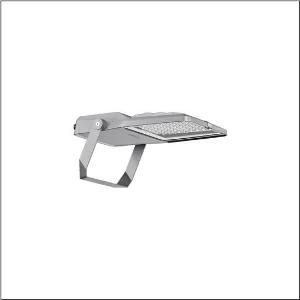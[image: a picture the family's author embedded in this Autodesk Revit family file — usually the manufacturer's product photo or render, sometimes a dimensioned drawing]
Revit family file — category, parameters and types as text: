
# Revit family: floodlight_fl_21_iq_mini___rs12_5xa7771c4b1a_004d
name_source: partatom
category: Lighting Fixtures
units: mm (PartAtom-declared; Revit-internal decimal feet)

## family parameters
Cut with Voids When Loaded = No
Host = Face
Light Source = No
Part Type = Normal
Room Calculation Point = No
Round Connector Dimension = Use Diameter
Shared = No

## types (1)
- --- (1 x LED, 12860 lm, 87.2 W, 4000K)
    Apparent Load = 87 VA
    CIE Flux Codes = 79 92 99 100 100
    Color Rendering = 70
    Color Temperature = 4000K
    Default Elevation = 1800 mm
    Description = Floodlight FL 21 iQ mini, floodlight, primary light control with lens, of PMMA, primary optical cover: protective disc, of toughened safety glass, transparent, light distribution: RS12, light emission: direct distribution, installation type: surface-mounted, LED, High Power LED, rated luminous flux: 12.860lm, luminous efficacy: 148lm/W, light colour: 740, colour temperature: 4000K, control: Auto-Match, Temp-Guard, Lumen-Switch, Night-Set, Smart-Wire, Light-Fading, Desk-Remote (wireless, voltage-free reading and setting of iQ features in the workshop via application-optimized NFC function/RFID function), optimised constant luminous flux control (CLO 2.0), with terminal, 6-pole, mains connection: 220..240V, AC, 50/60Hz, start of lifetime: 87W, end of service life: 92W, reduction: 40W, luminaire housing, of diecast aluminium, powder-coated, Siteco® metallic grey (DB 702S), corrosivity category C5 mid according to DIN EN ISO 12944, sealing non-destructively replaceable, mounting bracket, of steel, galvanised, powder-coated, Siteco® metallic grey (DB 702S), protection rating (complete): IP66, insulation class (complete): insulation class II (safety insulation), certification: CE, ENEC, VDE, protection symbol: D, impact resistance: IK08, permissible operating ambient temperature: -40..+40°C, permissible operating ambient temperature for outdoor applications: -40..+50°C, standard: DIN EN 12944, LABS conformity tested according to VDMA 24364:2018-05, packaging unit: 1 piece

Light Distribution: RS12
    Height = 70 mm
    Lamp = 1 x LED
    Lamp Light Flux = 12860 lm
    Lamp Power = 87.2 W
    Lamp count = 1
    Length = 485 mm
    Luminous efficacy = 147 lm/W
    Manufacturer = Siteco
    ModVariant = No
    Model = 5XA7771C4B1A
    Number of Poles = 1
    OnlyDefault = Yes
    Power Factor = 1
    Product Name = Floodlight FL 21 iQ mini | RS12
    Product group = floodlight | pylon annexe
    ProductGroupID = 6200
    Protection Class = Protection class II
    Protection Degree = IP 66
    RLX_Detail_Level = 1
    RLX_Emergency_Light_Flux = 0 lm
    RLX_Emergency_Type = 0
    RLX_Emergency_Type_DB = No
    RlxData = <blob elided: 90961 chars, md5=820a6b4f>
    Socket = socket
    Standby Power = 0 W
    System Light Flux = 12860 lm
    System Power = 87 W
    Type Comments = factory setting: luminous flux: 100 % | dim-lin: 254 | 456 mA
    Type Image = l_1006845.jpg
    URL = http://relux.com
    VarID = @adj_100023
    Voltage = 0 V
    Weight = 0.00 kg
    Width = 337 mm

## geometry (parser evidence)
native form markers: Blend x4, Sweep x14
no freeform markers — native parametric forms only
